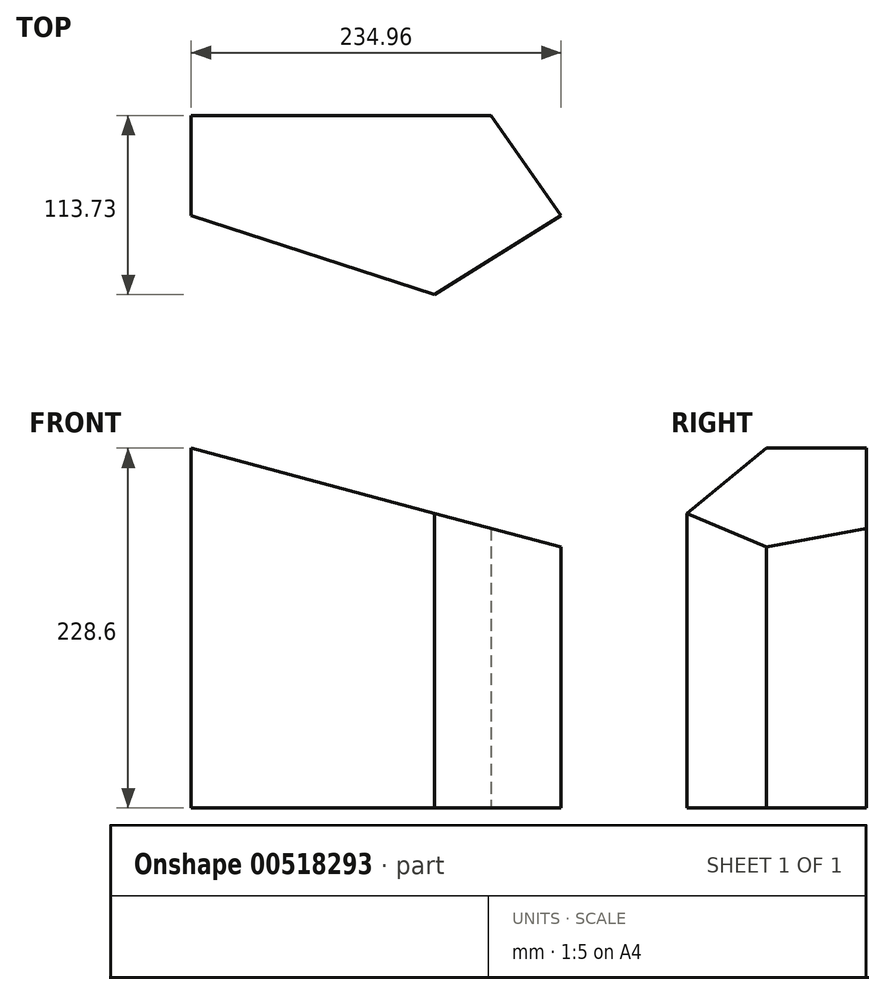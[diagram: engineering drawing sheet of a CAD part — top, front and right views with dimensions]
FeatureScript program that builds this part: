
annotation { "Feature Type Name" : "Feature", "Feature Type Description" : "" }
export const myFeature = defineFeature(function(context is Context, id is Id, definition is map)
    precondition{}
    {
        {
            var Q0;
            Q0=qCreatedBy(makeId("Top.planeOp"),FACE);
            var sketch = newSketch(context, id + "F0", { "sketchPlane" : qUnion([Q0])});
            skLineSegment(sketch, "E0", {"start": v(35.92, 63.5) * mm, "end": v(-154.58, 63.5) * mm});
            skLineSegment(sketch, "E1", {"start": v(-154.58, 63.5) * mm, "end": v(-154.58, 0) * mm});
            skLineSegment(sketch, "E2", {"start": v(-154.58, 0) * mm, "end": v(0, -50.23) * mm});
            skLineSegment(sketch, "E3", {"start": v(0, -50.23) * mm, "end": v(80.38, 0) * mm});
            skLineSegment(sketch, "E4", {"start": v(80.38, 0) * mm, "end": v(35.92, 63.5) * mm});
            skSolve(sketch);
        }
        {
            var Q0;
            Q0=makeQuery(id+"F0.imprint","IMPRINT",FACE,{"disambiguationData":[TD([[makeQuery(id+"F0.imprint","IMPRINT",EDGE,{"derivedFrom":sQuery(id+"F0.wireOp",EDGE,"E0")}),1.0]])]});
            extrude(context, id + "F1", {"entities" : qUnion([Q0]), "depth" : 228.6 * mm, "offsetDistance" : 25.4 * mm});
        }
        {
            var Q0;
            Q0=qCreatedBy(makeId("Front.planeOp"),FACE);
            var sketch = newSketch(context, id + "F2", { "sketchPlane" : qUnion([Q0])});
            skLineSegment(sketch, "E5", {"start": v(-154.58, 228.6) * mm, "end": v(111.74, 157.24) * mm});
            skLineSegment(sketch, "E6", {"start": v(111.74, 157.24) * mm, "end": v(111.74, 289.72) * mm});
            skLineSegment(sketch, "E7", {"start": v(111.74, 289.72) * mm, "end": v(-154.58, 289.72) * mm});
            skLineSegment(sketch, "E8", {"start": v(-154.58, 289.72) * mm, "end": v(-154.58, 228.6) * mm});
            skSolve(sketch);
        }
        {
            var Q0;
            Q0=makeQuery(id+"F2.imprint","IMPRINT",FACE,{"disambiguationData":[TD([[makeQuery(id+"F2.imprint","IMPRINT",EDGE,{"derivedFrom":sQuery(id+"F2.wireOp",EDGE,"E5")}),1.0]])]});
            extrude(context, id + "F3", {"entities" : qUnion([Q0]), "operationType" : NewBodyOperationType.REMOVE, "endBound" : BoundingType.SYMMETRIC, "oppositeDirection" : true, "depth" : 228.6 * mm, "offsetDistance" : 25.4 * mm});
        }
    });
